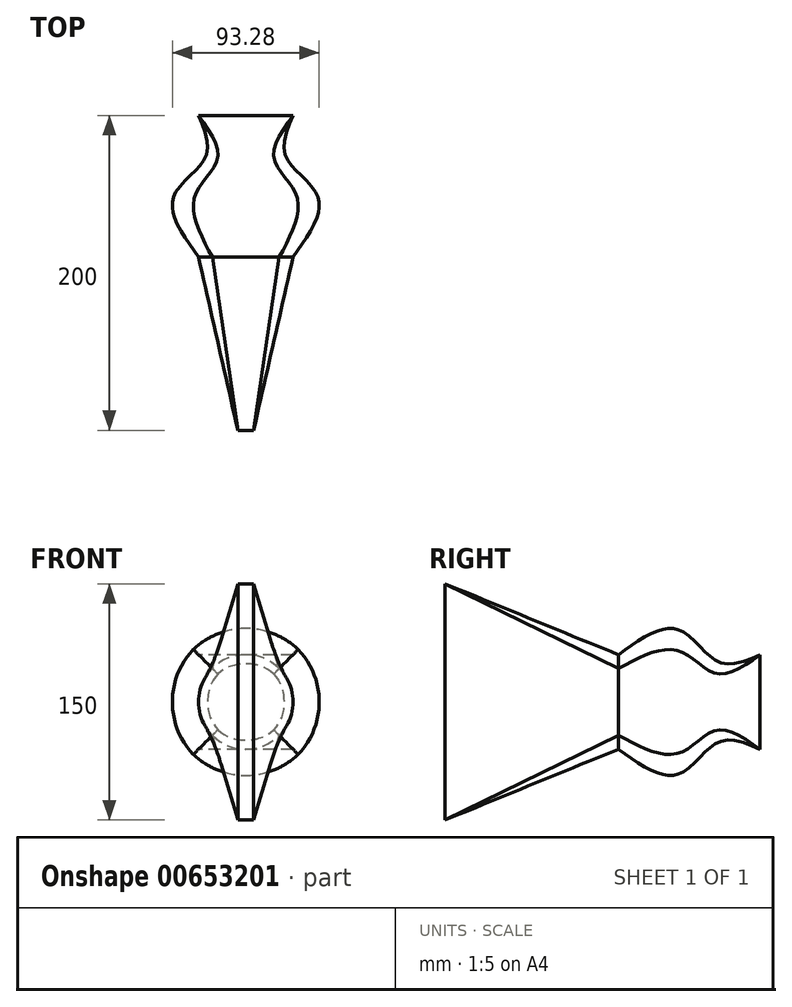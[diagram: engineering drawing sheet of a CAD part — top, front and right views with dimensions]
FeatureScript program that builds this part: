
annotation { "Feature Type Name" : "Feature", "Feature Type Description" : "" }
export const myFeature = defineFeature(function(context is Context, id is Id, definition is map)
    precondition{}
    {
        {
            var Q0;
            Q0=qCreatedBy(makeId("Front.planeOp"),FACE);
            cPlane(context, id + "F0", {"entities" : qUnion([Q0]), "cplaneType" : CPlaneType.OFFSET, "offset" : 25 * mm, "width" : 150 * mm, "height" : 150 * mm});
        }
        {
            var Q0;
            Q0=qCreatedBy(id+"F0.planeOp",FACE);
            cPlane(context, id + "F1", {"entities" : qUnion([Q0]), "cplaneType" : CPlaneType.OFFSET, "offset" : 25 * mm, "width" : 150 * mm, "height" : 150 * mm});
        }
        {
            var Q0;
            Q0=qCreatedBy(id+"F1.planeOp",FACE);
            cPlane(context, id + "F2", {"entities" : qUnion([Q0]), "cplaneType" : CPlaneType.OFFSET, "offset" : 40 * mm, "width" : 150 * mm, "height" : 150 * mm});
        }
        {
            var Q0;
            Q0=qCreatedBy(makeId("Front.planeOp"),FACE);
            var sketch = newSketch(context, id + "F3", { "sketchPlane" : qUnion([Q0])});
            skLineSegment(sketch, "E0.bottom", {"start": v(30, -30) * mm, "end": v(-30, -30) * mm});
            skLineSegment(sketch, "E0.top", {"start": v(30, 30) * mm, "end": v(-30, 30) * mm});
            skLineSegment(sketch, "E0.left", {"start": v(30, -30) * mm, "end": v(30, 30) * mm});
            skLineSegment(sketch, "E0.right", {"start": v(-30, -30) * mm, "end": v(-30, 30) * mm});
            skPoint(sketch, "E0.middle", {"position": v(0, 0) * mm});
            skSolve(sketch);
        }
        {
            var Q0;
            Q0=qCreatedBy(id+"F0.planeOp",FACE);
            var sketch = newSketch(context, id + "F4", { "sketchPlane" : qUnion([Q0])});
            skCircle(sketch, "E1", {"center": v(0, 0) * mm, "radius": 25 * mm});
            skSolve(sketch);
        }
        {
            var Q0;
            Q0=qCreatedBy(id+"F1.planeOp",FACE);
            var sketch = newSketch(context, id + "F5", { "sketchPlane" : qUnion([Q0])});
            skCircle(sketch, "E2", {"center": v(0, 0) * mm, "radius": 45.14 * mm});
            skSolve(sketch);
        }
        {
            var Q0;
            Q0=qCreatedBy(id+"F2.planeOp",FACE);
            var sketch = newSketch(context, id + "F6", { "sketchPlane" : qUnion([Q0])});
            skCircle(sketch, "E3", {"center": v(0, 0) * mm, "radius": 30 * mm});
            skSolve(sketch);
        }
        {
            var Q0;
            Q0 = qSketchRegion(id + "F6", true);
            var Q1;
            Q1 = qSketchRegion(id + "F5", true);
            var Q2;
            Q2 = qSketchRegion(id + "F4", true);
            var Q3;
            Q3 = qSketchRegion(id + "F3", true);
            loft(context, id + "F7", {"sheetProfilesArray" : [{ "sheetProfileEntities" : qUnion([Q0]) }, { "sheetProfileEntities" : qUnion([Q1]) }, { "sheetProfileEntities" : qUnion([Q2]) }, { "sheetProfileEntities" : qUnion([Q3]) }]});
        }
        {
            var Q0;
            Q0=qCreatedBy(makeId("Front.planeOp"),FACE);
            cPlane(context, id + "F8", {"entities" : qUnion([Q0]), "cplaneType" : CPlaneType.OFFSET, "offset" : 200 * mm, "width" : 150 * mm, "height" : 150 * mm});
        }
        {
            var Q0;
            Q0=qCreatedBy(id+"F8.planeOp",FACE);
            var sketch = newSketch(context, id + "F9", { "sketchPlane" : qUnion([Q0])});
            skLineSegment(sketch, "E4.bottom", {"start": v(5, 75) * mm, "end": v(-5, 75) * mm});
            skLineSegment(sketch, "E4.top", {"start": v(5, -75) * mm, "end": v(-5, -75) * mm});
            skLineSegment(sketch, "E4.left", {"start": v(5, 75) * mm, "end": v(5, -75) * mm});
            skLineSegment(sketch, "E4.right", {"start": v(-5, 75) * mm, "end": v(-5, -75) * mm});
            skPoint(sketch, "E4.middle", {"position": v(0, 0) * mm});
            skSolve(sketch);
        }
        {
            var Q1;
            Q1=makeQuery(id+"F7.opLoft","CAP_FACE",FACE,{"disambiguationData":[OSD([makeQuery(id+"F6.imprint","IMPRINT",FACE,{"disambiguationData":[TD([[makeQuery(id+"F6.imprint","IMPRINT",EDGE,{"derivedFrom":sQuery(id+"F6.wireOp",EDGE,"E3")}),1.0]])]})])],"isStart":true});
            var Q2;
            Q2=makeQuery(id+"F9.imprint","IMPRINT",FACE,{"disambiguationData":[TD([[makeQuery(id+"F9.imprint","IMPRINT",EDGE,{"derivedFrom":sQuery(id+"F9.wireOp",EDGE,"E4.bottom")}),1.0]])]});
            loft(context, id + "F10", {"operationType" : NewBodyOperationType.ADD, "sheetProfilesArray" : [{ "sheetProfileEntities" : qUnion([Q1]) }, { "sheetProfileEntities" : qUnion([Q2]) }]});
        }
    });
